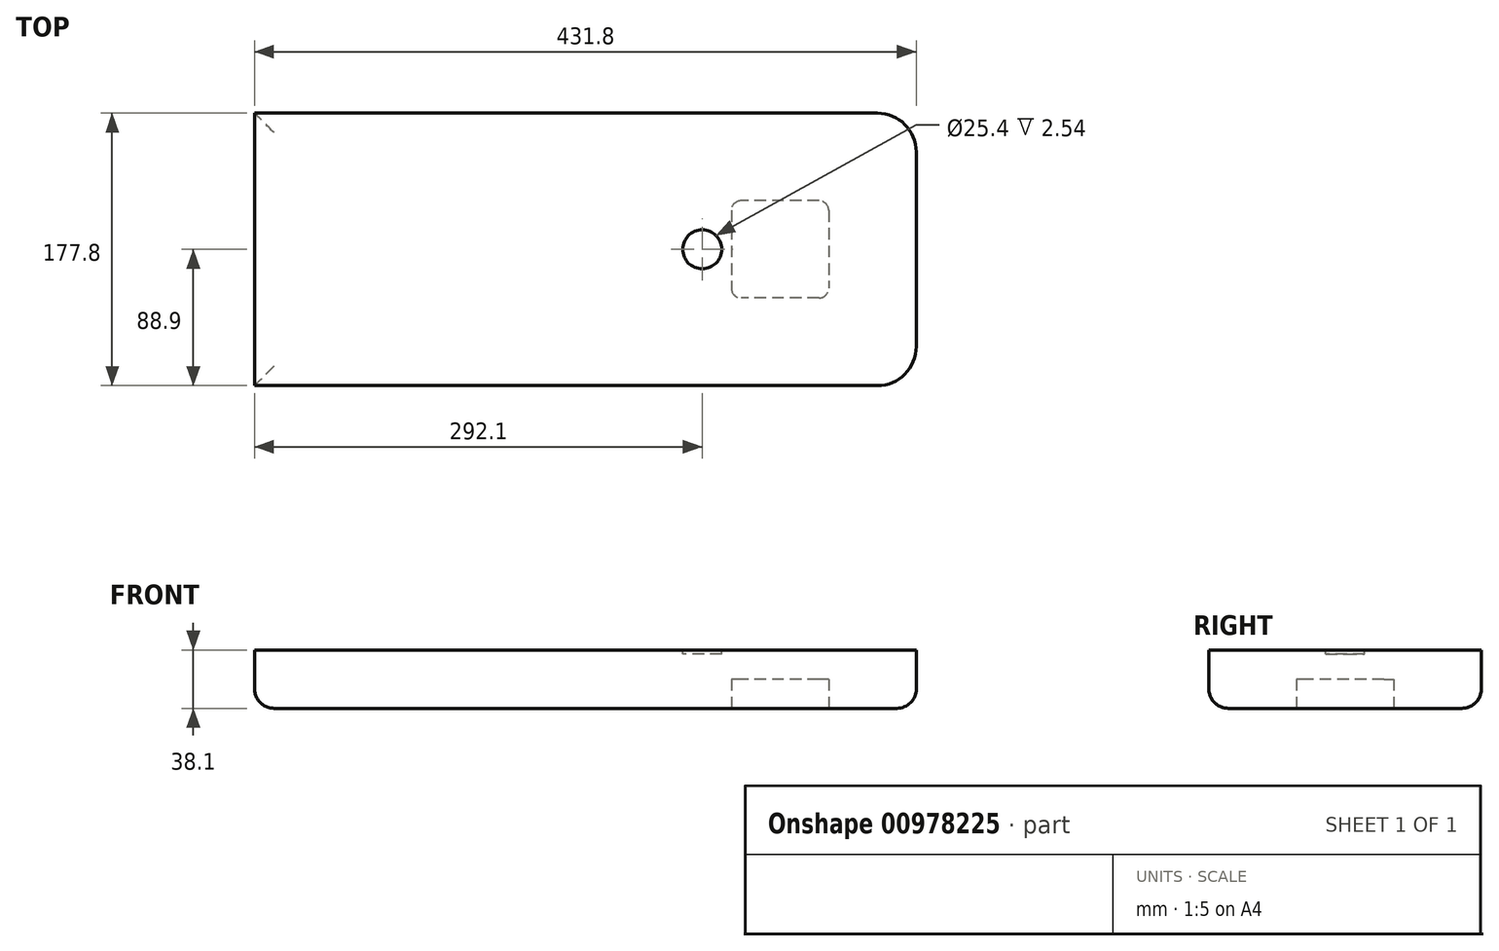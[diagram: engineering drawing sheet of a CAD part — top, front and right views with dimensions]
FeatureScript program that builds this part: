
annotation { "Feature Type Name" : "Feature", "Feature Type Description" : "" }
export const myFeature = defineFeature(function(context is Context, id is Id, definition is map)
    precondition{}
    {
        {
            var Q0;
            Q0=qCreatedBy(makeId("Top.planeOp"),FACE);
            var sketch = newSketch(context, id + "F0", { "sketchPlane" : qUnion([Q0])});
            skLineSegment(sketch, "E0.bottom", {"start": v(-88.9, 88.9) * mm, "end": v(88.9, 88.9) * mm});
            skLineSegment(sketch, "E0.top", {"start": v(-88.9, -88.9) * mm, "end": v(88.9, -88.9) * mm});
            skLineSegment(sketch, "E0.left", {"start": v(-88.9, 88.9) * mm, "end": v(-88.9, -88.9) * mm});
            skLineSegment(sketch, "E0.right", {"start": v(88.9, 88.9) * mm, "end": v(88.9, -88.9) * mm});
            skLineSegment(sketch, "E1", {"start": v(0, 0) * mm, "end": v(0, 88.9) * mm, "construction": true});
            skLineSegment(sketch, "E2", {"start": v(0, 0) * mm, "end": v(88.9, 0) * mm, "construction": true});
            skSolve(sketch);
        }
        {
            var Q0;
            Q0=makeQuery(id+"F0.imprint","IMPRINT",FACE,{"disambiguationData":[TD([[makeQuery(id+"F0.imprint","IMPRINT",EDGE,{"derivedFrom":sQuery(id+"F0.wireOp",EDGE,"E0.bottom")}),-1.0]])]});
            extrude(context, id + "F1", {"entities" : qUnion([Q0]), "oppositeDirection" : true, "depth" : 38.1 * mm, "offsetDistance" : 25.4 * mm});
        }
        {
            var Q0;
            Q0=makeQuery(id+"F1.opExtrude","SWEPT_FACE",FACE,{"disambiguationData":[OSD([sQuery(id+"F0.wireOp",EDGE,"E0.left")])]});
            var sketch = newSketch(context, id + "F2", { "sketchPlane" : qUnion([Q0])});
            skSolve(sketch);
        }
        {
            var Q0;
            {var subQ0=sQuery(id+"F0.wireOp",EDGE,"E0.left");Q0=makeQuery(id+"F2.imprint","IMPRINT",FACE,{"disambiguationData":[TD([[makeQuery(id+"F2.imprint","IMPRINT",EDGE,{"derivedFrom":makeQuery(id+"F1.opExtrude","CAP_EDGE",EDGE,{"disambiguationData":[OSD([subQ0])],"isStart":true})}),-1.0]])]});}
            extrude(context, id + "F3", {"entities" : qUnion([Q0]), "operationType" : NewBodyOperationType.ADD, "depth" : 254 * mm, "offsetDistance" : 25.4 * mm});
        }
        {
            var Q0;
            Q0=makeQuery(id+"F1.opExtrude","SWEPT_EDGE",EDGE,{"disambiguationData":[OSD([sQuery(id+"F0.wireOp",EDGE,"E0.top"),sQuery(id+"F0.wireOp",EDGE,"E0.left")])]});
            var Q1;
            Q1=makeQuery(id+"F1.opExtrude","SWEPT_EDGE",EDGE,{"disambiguationData":[OSD([sQuery(id+"F0.wireOp",EDGE,"E0.bottom"),sQuery(id+"F0.wireOp",EDGE,"E0.left")])]});
            var Q2;
            Q2=makeQuery(id+"F1.opExtrude","SWEPT_EDGE",EDGE,{"disambiguationData":[OSD([sQuery(id+"F0.wireOp",EDGE,"E0.bottom"),sQuery(id+"F0.wireOp",EDGE,"E0.right")])]});
            var Q3;
            Q3=makeQuery(id+"F1.opExtrude","SWEPT_EDGE",EDGE,{"disambiguationData":[OSD([sQuery(id+"F0.wireOp",EDGE,"E0.top"),sQuery(id+"F0.wireOp",EDGE,"E0.right")])]});
            fillet(context, id + "F4", {"entities" : qUnion([Q0, Q1, Q2, Q3]), "radius" : 25.4 * mm, "tangentPropagation" : true, "allowEdgeOverflow" : false});
        }
        {
            var Q0;
            Q0=makeQuery(id+"F1.opExtrude","CAP_EDGE",EDGE,{"disambiguationData":[OSD([sQuery(id+"F0.wireOp",EDGE,"E0.top")])],"isStart":false});
            var Q1;
            {var subQ0=sQuery(id+"F0.wireOp",EDGE,"E0.left");Q1=makeQuery(id+"F3.opExtrude","CAP_EDGE",EDGE,{"disambiguationData":[OSD([subQ0]),TDD([makeQuery(id+"F2.imprint","IMPRINT",EDGE,{"derivedFrom":makeQuery(id+"F1.opExtrude","CAP_EDGE",EDGE,{"disambiguationData":[OSD([subQ0])],"isStart":false})})])],"isStart":false});}
            fillet(context, id + "F5", {"entities" : qUnion([Q0, Q1]), "radius" : 12.7 * mm, "tangentPropagation" : true, "allowEdgeOverflow" : false});
        }
        {
            var Q0;
            Q0=makeQuery(id+"F1.opExtrude","CAP_FACE",FACE,{"disambiguationData":[OSD([sQuery(id+"F0.wireOp",EDGE,"E0.bottom"),sQuery(id+"F0.wireOp",EDGE,"E0.top"),sQuery(id+"F0.wireOp",EDGE,"E0.left"),sQuery(id+"F0.wireOp",EDGE,"E0.right")])],"isStart":false});
            var sketch = newSketch(context, id + "F6", { "sketchPlane" : qUnion([Q0])});
            skLineSegment(sketch, "E3.bottom", {"start": v(25.4, -31.75) * mm, "end": v(-25.4, -31.75) * mm});
            skLineSegment(sketch, "E3.top", {"start": v(25.4, 31.75) * mm, "end": v(-25.4, 31.75) * mm});
            skLineSegment(sketch, "E3.left", {"start": v(31.75, -25.4) * mm, "end": v(31.75, 25.4) * mm});
            skLineSegment(sketch, "E3.right", {"start": v(-31.75, -25.4) * mm, "end": v(-31.75, 25.4) * mm});
            skPoint(sketch, "E3.middle", {"position": v(0, 0) * mm});
            skPoint(sketch, "E4.visualSharp", {"position": v(-31.75, 31.75) * mm});
            skArc(sketch, "E4.filletArc", {"start": v(-25.4, 31.75) * mm, "mid": v(-29.9, 29.9) * mm, "end": v(-31.75, 25.4) * mm});
            skPoint(sketch, "E5.visualSharp", {"position": v(31.75, 31.75) * mm});
            skArc(sketch, "E5.filletArc", {"start": v(31.75, 25.4) * mm, "mid": v(29.9, 29.9) * mm, "end": v(25.4, 31.75) * mm});
            skPoint(sketch, "E6.visualSharp", {"position": v(31.75, -31.75) * mm});
            skArc(sketch, "E6.filletArc", {"start": v(25.4, -31.75) * mm, "mid": v(29.9, -29.9) * mm, "end": v(31.75, -25.4) * mm});
            skPoint(sketch, "E7.visualSharp", {"position": v(-31.75, -31.75) * mm});
            skArc(sketch, "E7.filletArc", {"start": v(-31.75, -25.4) * mm, "mid": v(-29.9, -29.9) * mm, "end": v(-25.4, -31.75) * mm});
            skSolve(sketch);
        }
        {
            var Q0;
            Q0 = qSketchRegion(id + "F6", true);
            extrude(context, id + "F7", {"entities" : qUnion([Q0]), "operationType" : NewBodyOperationType.REMOVE, "oppositeDirection" : true, "depth" : 19.05 * mm, "offsetDistance" : 25.4 * mm});
        }
        {
            var Q0;
            Q0=makeQuery(id+"F1.opExtrude","CAP_FACE",FACE,{"disambiguationData":[OSD([sQuery(id+"F0.wireOp",EDGE,"E0.bottom"),sQuery(id+"F0.wireOp",EDGE,"E0.top"),sQuery(id+"F0.wireOp",EDGE,"E0.left"),sQuery(id+"F0.wireOp",EDGE,"E0.right")])],"isStart":true});
            var sketch = newSketch(context, id + "F8", { "sketchPlane" : qUnion([Q0])});
            skCircle(sketch, "E8", {"center": v(-50.8, 0) * mm, "radius": 12.7 * mm});
            skSolve(sketch);
        }
        {
            var Q0;
            Q0 = qSketchRegion(id + "F8", true);
            extrude(context, id + "F9", {"entities" : qUnion([Q0]), "operationType" : NewBodyOperationType.REMOVE, "oppositeDirection" : true, "depth" : 2.54 * mm, "offsetDistance" : 25.4 * mm});
        }
    });
